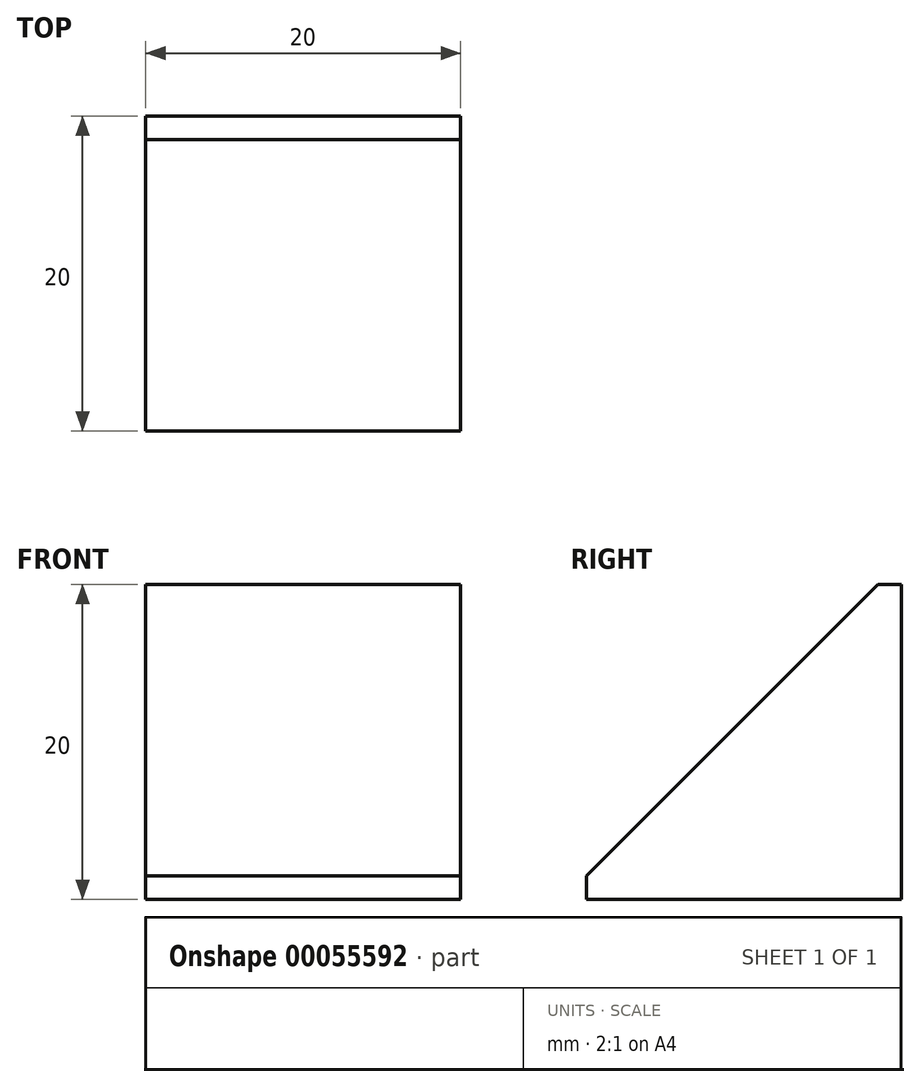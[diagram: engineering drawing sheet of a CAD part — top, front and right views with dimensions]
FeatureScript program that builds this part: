
annotation { "Feature Type Name" : "Feature", "Feature Type Description" : "" }
export const myFeature = defineFeature(function(context is Context, id is Id, definition is map)
    precondition{}
    {
        {
            var Q0;
            Q0=qCreatedBy(makeId("Right.planeOp"),FACE);
            var sketch = newSketch(context, id + "F0", { "sketchPlane" : qUnion([Q0]), "asVersion" : FeatureScriptVersionNumber.V275_SKETCH_PATTERN_LOWER_LIMIT});
            skLineSegment(sketch, "E0", {"start": v(0, 0) * mm, "end": v(0, 20) * mm});
            skLineSegment(sketch, "E1", {"start": v(0, 20) * mm, "end": v(-1.5, 20) * mm});
            skLineSegment(sketch, "E2", {"start": v(-1.5, 20) * mm, "end": v(-20, 1.5) * mm});
            skLineSegment(sketch, "E3", {"start": v(-20, 1.5) * mm, "end": v(-20, 0) * mm});
            skLineSegment(sketch, "E4", {"start": v(-20, 0) * mm, "end": v(0, 0) * mm});
            skSolve(sketch);
        }
        {
            var Q0;
            Q0=makeQuery(id+"F0.imprint","IMPRINT",FACE,{"disambiguationData":[TD([[makeQuery(id+"F0.imprint","IMPRINT",EDGE,{"derivedFrom":sQuery(id+"F0.wireOp",EDGE,"E0")}),1.0]])]});
            extrude(context, id + "F1", {"entities" : qUnion([Q0]), "endBound" : BoundingType.SYMMETRIC, "depth" : 20 * mm});
        }
    });
